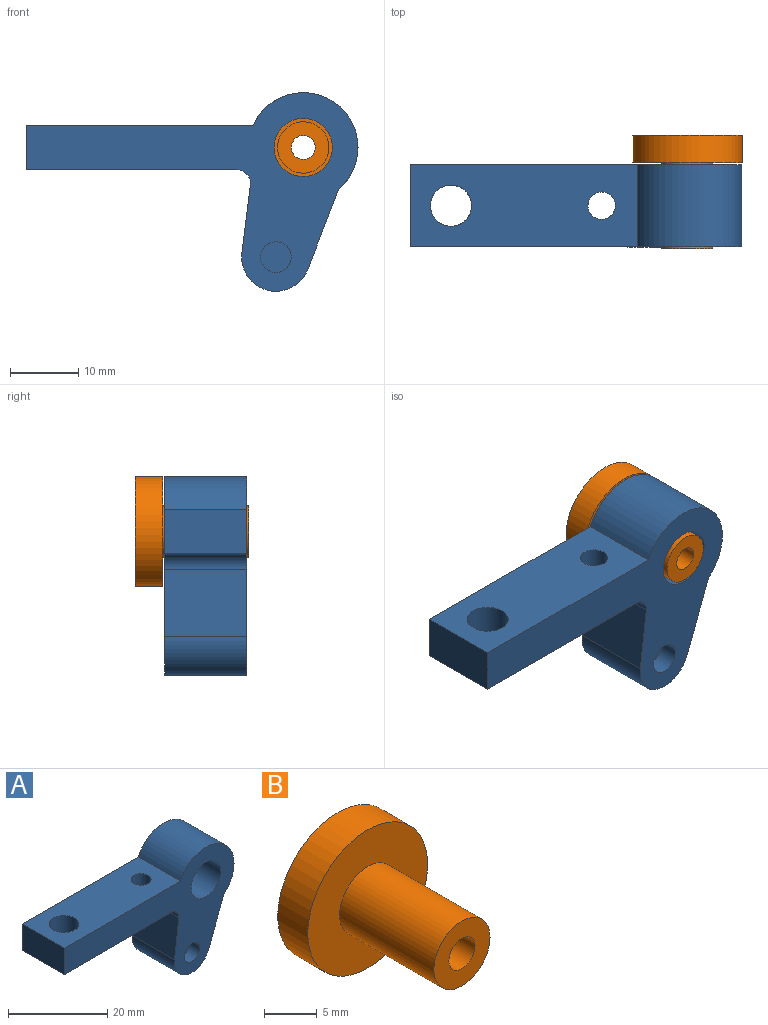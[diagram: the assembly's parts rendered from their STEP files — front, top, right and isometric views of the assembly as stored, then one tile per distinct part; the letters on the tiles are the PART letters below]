
ASSEMBLY  parts=2 mates=1
PART A: 24 faces, bbox 48.5x12x29 mm
  f0: cylinder r=2mm len=6.5mm, axis (0,0,1), area 81.7mm2, adj f12,f14
  f1: cylinder r=3mm len=6.5mm, axis (0,0,1), area 122.5mm2, adj f12,f14
  f2: cylinder r=2mm len=12mm, axis (0,-1,0), area 40.6mm2, adj f7,f9,f10,f12
  f3: cylinder r=4.25mm len=12mm, axis (0,1,0), area 320.4mm2, adj f9,f10
  f4: cylinder r=5mm len=12mm, axis (0,1,0), area 173.9mm2, adj f7,f8,f9,f10
  f5: cylinder r=2.25mm len=9mm, axis (0,1,0), area 127.2mm2, adj f10,f16
  f6: cylinder r=2.25mm len=4.5mm, axis (0,1,0), area 39.6mm2, adj f9,f15
  f7: plane 12x9.9mm, normal (-0.99,0,0.12), area 119.7mm2, adj f2,f4,f9,f10
  f8: plane 12x11.68mm, normal (0.93,0,-0.36), area 150.1mm2, adj f4,f9,f10,f13
  f9: plane 48.5x29.01mm, normal (0,-1,0), area 487.5mm2, adj f2,f3,f4,f6,f7,f8,f11,f12
  f10: plane 48.5x29.01mm, normal (0,1,0), area 487.5mm2, adj f2,f3,f4,f5,f7,f8,f11,f12
  f11: plane 12x6.5mm, normal (-1,0,0), area 78mm2, adj f9,f10,f12,f14
  f12: plane 30.78x12mm, normal (0,0,-1), area 328.6mm2, adj f0,f1,f2,f9,f10,f11
  f13: cylinder r=8mm len=15.31mm, axis (0,1,0), area 345.1mm2, adj f8,f9,f10,f14
  f14: plane 33.19x12mm, normal (0,0,1), area 357.4mm2, adj f0,f1,f9,f10,f11,f13
  f15: plane 4.5x4.5mm, normal (0,-1,0), area 15.9mm2, adj f6
  f16: plane 4.5x4.5mm, normal (0,1,0), area 15.9mm2, adj f5
  f17: cylinder r=4.5mm len=8.7mm, axis (0,1,0), area 78.3mm2, adj f20,f21,f22,f23
  f18: cylinder r=2.75mm len=6mm, axis (0,1,0), area 103.7mm2, adj f21,f23
  f19: plane 11.04x6mm, normal (0,0,-1), area 66.2mm2, adj f20,f21,f22,f23
  f20: plane 6x5.95mm, normal (0.99,0,-0.12), area 36mm2, adj f17,f19,f21,f23
  f21: plane 11.81x11mm, normal (0,-1,0), area 74.5mm2, adj f17,f18,f19,f20,f22
  f22: plane 8.11x6mm, normal (-0.93,0,0.36), area 52.1mm2, adj f17,f19,f21,f23
  f23: plane 11.81x11mm, normal (0,1,0), area 74.5mm2, adj f17,f18,f19,f20,f22
PART B: 6 faces, bbox 16x16.6x16 mm
  f0: cylinder r=1.75mm len=16.6mm, axis (0,-1,0), area 182.5mm2, adj f4,f5
  f1: cylinder r=3.75mm len=12.6mm, axis (0,1,0), area 296.9mm2, adj f3,f5
  f2: cylinder r=8mm len=16mm, axis (0,1,0), area 201.1mm2, adj f3,f4
  f3: plane 16x16mm, normal (0,-1,0), area 156.9mm2, adj f1,f2
  f4: plane 16x16mm, normal (0,1,0), area 191.4mm2, adj f0,f2
  f5: plane 7.5x7.5mm, normal (0,-1,0), area 34.6mm2, adj f0,f1
PLACE A at identity fixed
PLACE B t=(40.5,4.3,3.25)mm
MATE revolute B.f2 <-> A.f3  axis (0,1,0) through (40.5,-6,3.25)mm
